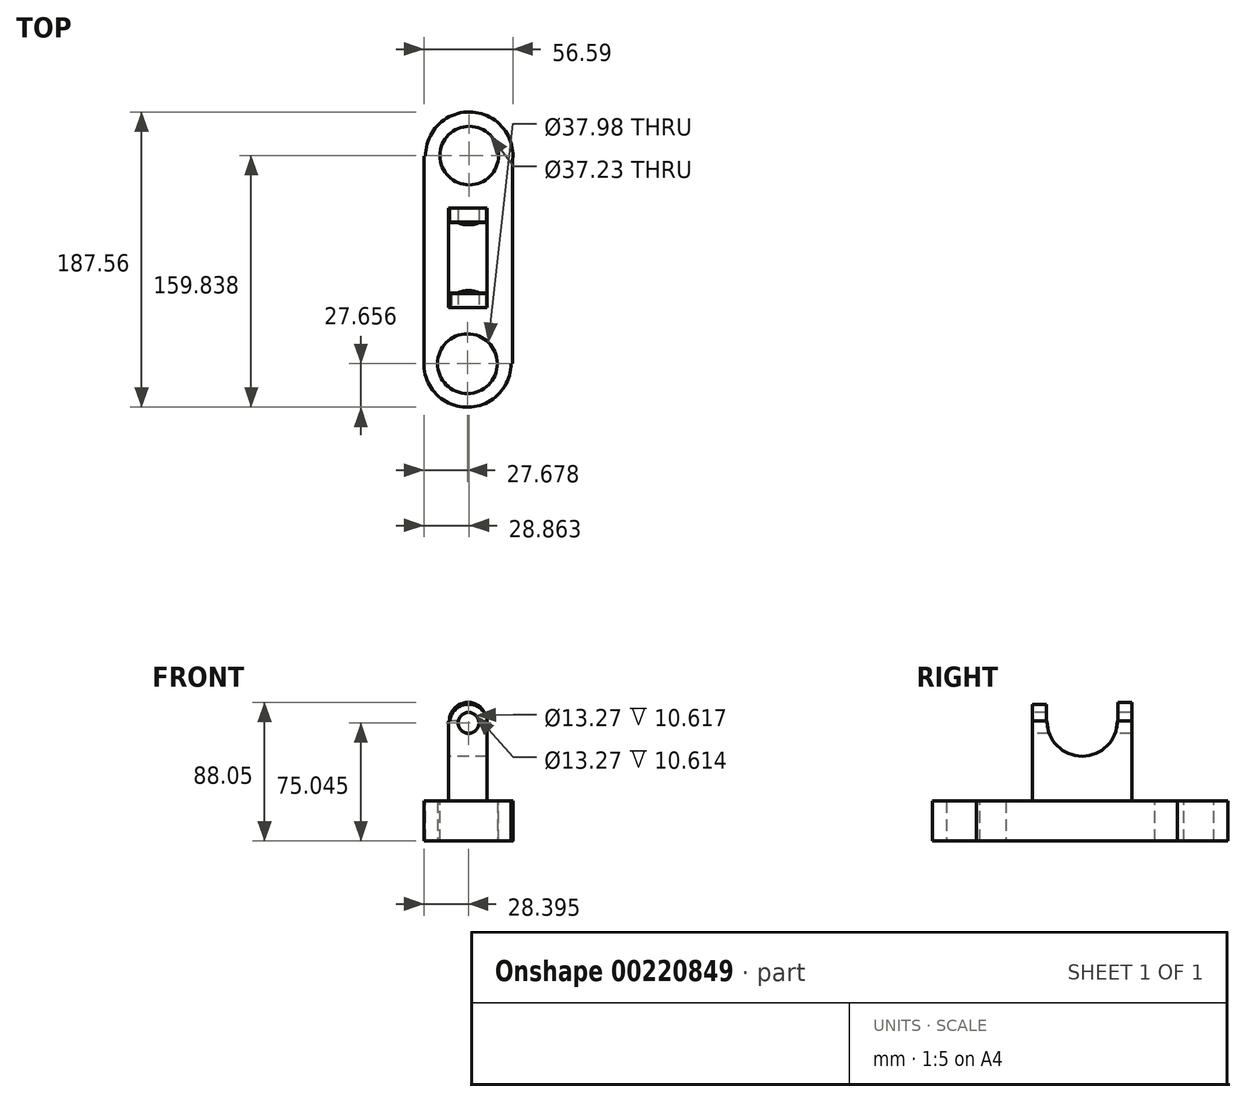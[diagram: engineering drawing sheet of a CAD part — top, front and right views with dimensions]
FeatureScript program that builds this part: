
annotation { "Feature Type Name" : "Feature", "Feature Type Description" : "" }
export const myFeature = defineFeature(function(context is Context, id is Id, definition is map)
    precondition{}
    {
        {
            var Q0;
            Q0=qCreatedBy(makeId("Top.planeOp"),FACE);
            var sketch = newSketch(context, id + "F0", { "sketchPlane" : qUnion([Q0])});
            skLineSegment(sketch, "E0.bottom", {"start": v(-15.7, 58.3) * mm, "end": v(40.4, 58.3) * mm});
            skLineSegment(sketch, "E0.top", {"start": v(-15.7, -73.54) * mm, "end": v(40.4, -73.54) * mm});
            skLineSegment(sketch, "E0.left", {"start": v(-15.7, 58.3) * mm, "end": v(-15.7, -73.54) * mm});
            skLineSegment(sketch, "E0.right", {"start": v(40.4, 58.3) * mm, "end": v(40.4, -73.54) * mm});
            skSolve(sketch);
        }
        {
            var Q0;
            Q0 = qSketchRegion(id + "F0", true);
            extrude(context, id + "F1", {"entities" : qUnion([Q0]), "depth" : 25.4 * mm});
        }
        {
            var Q0;
            Q0=makeQuery(id+"F1.opExtrude","CAP_FACE",FACE,{"disambiguationData":[OSD([sQuery(id+"F0.wireOp",EDGE,"E0.bottom"),sQuery(id+"F0.wireOp",EDGE,"E0.top"),sQuery(id+"F0.wireOp",EDGE,"E0.left"),sQuery(id+"F0.wireOp",EDGE,"E0.right")])],"isStart":false});
            var sketch = newSketch(context, id + "F2", { "sketchPlane" : qUnion([Q0])});
            skSolve(sketch);
        }
        {
            var Q0;
            Q0=makeQuery(id+"F2.imprint","IMPRINT",FACE,{"disambiguationData":[TD([[makeQuery(id+"F2.imprint","IMPRINT",EDGE,{"derivedFrom":makeQuery(id+"F1.opExtrude","CAP_EDGE",EDGE,{"disambiguationData":[OSD([sQuery(id+"F0.wireOp",EDGE,"E0.bottom")])],"isStart":false})}),-1.0]])]});
            var sketch = newSketch(context, id + "F3", { "sketchPlane" : qUnion([Q0])});
            skCircle(sketch, "E1", {"center": v(11.78, 40.06) * mm, "radius": 8.7 * mm});
            skSolve(sketch);
        }
        {
            var Q0;
            Q0 = qSketchRegion(id + "F3", true);
            extrude(context, id + "F4", {"entities" : qUnion([Q0]), "operationType" : NewBodyOperationType.REMOVE, "oppositeDirection" : true, "depth" : 25.4 * mm});
        }
        {
            var Q0;
            Q0=makeQuery(id+"F2.imprint","IMPRINT",FACE,{"disambiguationData":[TD([[makeQuery(id+"F2.imprint","IMPRINT",EDGE,{"derivedFrom":makeQuery(id+"F1.opExtrude","CAP_EDGE",EDGE,{"disambiguationData":[OSD([sQuery(id+"F0.wireOp",EDGE,"E0.bottom")])],"isStart":false})}),-1.0]])]});
            var sketch = newSketch(context, id + "F5", { "sketchPlane" : qUnion([Q0])});
            skCircle(sketch, "E2", {"center": v(11.31, -57.84) * mm, "radius": 8.85 * mm});
            skSolve(sketch);
        }
        {
            var Q0;
            Q0 = qSketchRegion(id + "F5", true);
            extrude(context, id + "F6", {"entities" : qUnion([Q0]), "operationType" : NewBodyOperationType.REMOVE, "oppositeDirection" : true, "depth" : 25.4 * mm});
        }
        {
            var Q0;
            Q0=makeQuery(id+"F2.imprint","IMPRINT",FACE,{"disambiguationData":[TD([[makeQuery(id+"F2.imprint","IMPRINT",EDGE,{"derivedFrom":makeQuery(id+"F1.opExtrude","CAP_EDGE",EDGE,{"disambiguationData":[OSD([sQuery(id+"F0.wireOp",EDGE,"E0.bottom")])],"isStart":false})}),-1.0]])]});
            var sketch = newSketch(context, id + "F7", { "sketchPlane" : qUnion([Q0])});
            skLineSegment(sketch, "E3.bottom", {"start": v(0, 25.28) * mm, "end": v(24.48, 25.28) * mm});
            skLineSegment(sketch, "E3.top", {"start": v(0, -37.75) * mm, "end": v(24.48, -37.75) * mm});
            skLineSegment(sketch, "E3.left", {"start": v(0, 25.28) * mm, "end": v(0, -37.75) * mm});
            skLineSegment(sketch, "E3.right", {"start": v(24.48, 25.28) * mm, "end": v(24.48, -37.75) * mm});
            skSolve(sketch);
        }
        {
            var Q0;
            Q0 = qSketchRegion(id + "F7", true);
            extrude(context, id + "F8", {"entities" : qUnion([Q0]), "operationType" : NewBodyOperationType.ADD, "depth" : 50.8 * mm});
        }
        {
            var Q0;
            Q0=makeQuery(id+"F8.opExtrude","SWEPT_FACE",FACE,{"disambiguationData":[OSD([sQuery(id+"F7.wireOp",EDGE,"E3.left")])]});
            var sketch = newSketch(context, id + "F9", { "sketchPlane" : qUnion([Q0])});
            skCircle(sketch, "E4", {"center": v(6.23, 76.2) * mm, "radius": 22.3 * mm});
            skSolve(sketch);
        }
        {
            var Q0;
            Q0 = qSketchRegion(id + "F9", true);
            extrude(context, id + "F10", {"entities" : qUnion([Q0]), "operationType" : NewBodyOperationType.ADD, "depth" : 76.2 * mm});
        }
        {
            var Q0;
            Q0=makeQuery(id+"F10.opExtrude","CAP_FACE",FACE,{"disambiguationData":[OSD([sQuery(id+"F9.wireOp",EDGE,"E4")])],"isStart":false});
            extrude(context, id + "F11", {"entities" : qUnion([Q0]), "operationType" : NewBodyOperationType.REMOVE, "oppositeDirection" : true, "depth" : 127 * mm});
        }
        {
            var Q0;
            Q0=makeQuery(id+"F8.opExtrude","SWEPT_FACE",FACE,{"disambiguationData":[OSD([sQuery(id+"F7.wireOp",EDGE,"E3.top")])]});
            var sketch = newSketch(context, id + "F12", { "sketchPlane" : qUnion([Q0])});
            skCircle(sketch, "E5", {"center": v(12.58, 75.05) * mm, "radius": 10.75 * mm});
            skCircle(sketch, "E6", {"center": v(12.58, 75.05) * mm, "radius": 11.86 * mm});
            skSolve(sketch);
        }
        {
            var Q0;
            Q0 = qSketchRegion(id + "F12", true);
            extrude(context, id + "F13", {"entities" : qUnion([Q0]), "operationType" : NewBodyOperationType.ADD, "oppositeDirection" : true, "depth" : 8.9 * mm});
        }
        {
            var Q0;
            Q0=makeQuery(id+"F13.boolean.opBoolean","MERGE",FACE,{"derivedFrom":[makeQuery(id+"F8.opExtrude","SWEPT_FACE",FACE,{"disambiguationData":[OSD([sQuery(id+"F7.wireOp",EDGE,"E3.top")])]}),makeQuery(id+"F13.opExtrude","CAP_FACE",FACE,{"disambiguationData":[OSD([sQuery(id+"F12.wireOp",EDGE,"E5"),sQuery(id+"F12.wireOp",EDGE,"E6")])],"isStart":true})]});
            var sketch = newSketch(context, id + "F14", { "sketchPlane" : qUnion([Q0])});
            skCircle(sketch, "E7", {"center": v(12.58, 76.2) * mm, "radius": 10.67 * mm});
            skSolve(sketch);
        }
        {
            var Q0;
            Q0 = qSketchRegion(id + "F14", true);
            extrude(context, id + "F15", {"entities" : qUnion([Q0]), "operationType" : NewBodyOperationType.ADD, "oppositeDirection" : true, "depth" : 8.9 * mm});
        }
        {
            var Q0;
            Q0=makeQuery(id+"F8.opExtrude","SWEPT_FACE",FACE,{"disambiguationData":[OSD([sQuery(id+"F7.wireOp",EDGE,"E3.bottom")])]});
            var sketch = newSketch(context, id + "F16", { "sketchPlane" : qUnion([Q0])});
            skCircle(sketch, "E8", {"center": v(-12.24, 76.2) * mm, "radius": 11.85 * mm});
            skSolve(sketch);
        }
        {
            var Q0;
            Q0 = qSketchRegion(id + "F16", true);
            extrude(context, id + "F17", {"entities" : qUnion([Q0]), "operationType" : NewBodyOperationType.ADD, "oppositeDirection" : true, "depth" : 8.9 * mm});
        }
        {
            var Q0;
            Q0=makeQuery(id+"F15.boolean.opBoolean","MERGE",FACE,{"derivedFrom":[makeQuery(id+"F13.boolean.opBoolean","MERGE",FACE,{"derivedFrom":[makeQuery(id+"F8.opExtrude","SWEPT_FACE",FACE,{"disambiguationData":[OSD([sQuery(id+"F7.wireOp",EDGE,"E3.top")])]}),makeQuery(id+"F13.opExtrude","CAP_FACE",FACE,{"disambiguationData":[OSD([sQuery(id+"F12.wireOp",EDGE,"E5"),sQuery(id+"F12.wireOp",EDGE,"E6")])],"isStart":true})]}),makeQuery(id+"F15.opExtrude","CAP_FACE",FACE,{"disambiguationData":[OSD([sQuery(id+"F14.wireOp",EDGE,"E7")])],"isStart":true})]});
            var sketch = newSketch(context, id + "F18", { "sketchPlane" : qUnion([Q0])});
            skCircle(sketch, "E9", {"center": v(12.58, 76.2) * mm, "radius": 5.51 * mm});
            skSolve(sketch);
        }
        {
            var Q0;
            Q0 = qSketchRegion(id + "F18", true);
            extrude(context, id + "F19", {"entities" : qUnion([Q0]), "operationType" : NewBodyOperationType.REMOVE, "depth" : 304.8 * mm});
        }
        {
            var Q0;
            Q0=makeQuery(id+"F15.boolean.opBoolean","MERGE",FACE,{"derivedFrom":[makeQuery(id+"F13.boolean.opBoolean","MERGE",FACE,{"derivedFrom":[makeQuery(id+"F8.opExtrude","SWEPT_FACE",FACE,{"disambiguationData":[OSD([sQuery(id+"F7.wireOp",EDGE,"E3.top")])]}),makeQuery(id+"F13.opExtrude","CAP_FACE",FACE,{"disambiguationData":[OSD([sQuery(id+"F12.wireOp",EDGE,"E5"),sQuery(id+"F12.wireOp",EDGE,"E6")])],"isStart":true})]}),makeQuery(id+"F15.opExtrude","CAP_FACE",FACE,{"disambiguationData":[OSD([sQuery(id+"F14.wireOp",EDGE,"E7")])],"isStart":true})]});
            var sketch = newSketch(context, id + "F20", { "sketchPlane" : qUnion([Q0])});
            skCircle(sketch, "E10", {"center": v(12.58, 75.05) * mm, "radius": 6.63 * mm});
            skSolve(sketch);
        }
        {
            var Q0;
            Q0 = qSketchRegion(id + "F20", true);
            extrude(context, id + "F21", {"entities" : qUnion([Q0]), "operationType" : NewBodyOperationType.REMOVE, "oppositeDirection" : true, "depth" : 304.8 * mm});
        }
        {
            var Q0;
            Q0=makeQuery(id+"F2.imprint","IMPRINT",FACE,{"disambiguationData":[TD([[makeQuery(id+"F2.imprint","IMPRINT",EDGE,{"derivedFrom":makeQuery(id+"F1.opExtrude","CAP_EDGE",EDGE,{"disambiguationData":[OSD([sQuery(id+"F0.wireOp",EDGE,"E0.bottom")])],"isStart":false})}),-1.0]])]});
            var sketch = newSketch(context, id + "F22", { "sketchPlane" : qUnion([Q0])});
            skCircle(sketch, "E11", {"center": v(12, -73.78) * mm, "radius": 27.02 * mm});
            skSolve(sketch);
        }
        {
            var Q0;
            Q0=sQuery(id+"F22.wireOp",EDGE,"E11");
            extrude(context, id + "F23", {"bodyType" : ToolBodyType.SURFACE, "surfaceEntities" : qUnion([Q0]), "oppositeDirection" : true, "depth" : 25.4 * mm});
        }
        {
            var Q0;
            Q0=makeQuery(id+"F2.imprint","IMPRINT",FACE,{"disambiguationData":[TD([[makeQuery(id+"F2.imprint","IMPRINT",EDGE,{"derivedFrom":makeQuery(id+"F1.opExtrude","CAP_EDGE",EDGE,{"disambiguationData":[OSD([sQuery(id+"F0.wireOp",EDGE,"E0.bottom")])],"isStart":false})}),-1.0]])]});
            var sketch = newSketch(context, id + "F24", { "sketchPlane" : qUnion([Q0])});
            skCircle(sketch, "E12", {"center": v(11.87, -73.52) * mm, "radius": 18.97 * mm});
            skCircle(sketch, "E13", {"center": v(11.87, -73.52) * mm, "radius": 27.68 * mm});
            skSolve(sketch);
        }
        {
            var Q0;
            Q0 = qSketchRegion(id + "F24", true);
            extrude(context, id + "F25", {"entities" : qUnion([Q0]), "operationType" : NewBodyOperationType.ADD, "oppositeDirection" : true, "depth" : 25.4 * mm});
        }
        {
            var Q0;
            Q0=makeQuery(id+"F2.imprint","IMPRINT",FACE,{"disambiguationData":[TD([[makeQuery(id+"F2.imprint","IMPRINT",EDGE,{"derivedFrom":makeQuery(id+"F1.opExtrude","CAP_EDGE",EDGE,{"disambiguationData":[OSD([sQuery(id+"F0.wireOp",EDGE,"E0.bottom")])],"isStart":false})}),-1.0]])]});
            var sketch = newSketch(context, id + "F26", { "sketchPlane" : qUnion([Q0])});
            skLineSegment(sketch, "E14.bottom", {"start": v(12.84, -71.37) * mm, "end": v(0, -71.37) * mm});
            skLineSegment(sketch, "E14.top", {"start": v(12.84, -47.36) * mm, "end": v(0, -47.36) * mm});
            skLineSegment(sketch, "E14.left", {"start": v(12.84, -71.37) * mm, "end": v(12.84, -47.36) * mm});
            skLineSegment(sketch, "E14.right", {"start": v(0, -71.37) * mm, "end": v(0, -47.36) * mm});
            skLineSegment(sketch, "E15.bottom", {"start": v(12.84, -47.36) * mm, "end": v(20.45, -47.36) * mm});
            skLineSegment(sketch, "E15.top", {"start": v(12.84, -47.36) * mm, "end": v(20.45, -47.36) * mm});
            skLineSegment(sketch, "E15.left", {"start": v(12.84, -47.36) * mm, "end": v(12.84, -47.36) * mm});
            skLineSegment(sketch, "E15.right", {"start": v(20.45, -47.36) * mm, "end": v(20.45, -47.36) * mm});
            skLineSegment(sketch, "E16.top", {"start": v(12.84, -71.6) * mm, "end": v(20.45, -71.6) * mm});
            skLineSegment(sketch, "E16.left", {"start": v(12.84, -47.36) * mm, "end": v(12.84, -71.6) * mm});
            skLineSegment(sketch, "E16.right", {"start": v(20.45, -47.36) * mm, "end": v(20.45, -71.6) * mm});
            skSolve(sketch);
        }
        {
            var Q0;
            Q0 = qSketchRegion(id + "F26", true);
            extrude(context, id + "F27", {"entities" : qUnion([Q0]), "operationType" : NewBodyOperationType.ADD, "oppositeDirection" : true, "depth" : 25.4 * mm});
        }
        {
            var Q0;
            Q0=makeQuery(id+"F27.boolean.opBoolean","MERGE",FACE,{"derivedFrom":[makeQuery(id+"F25.boolean.opBoolean","MERGE",FACE,{"derivedFrom":[makeQuery(id+"F1.opExtrude","CAP_FACE",FACE,{"disambiguationData":[OSD([sQuery(id+"F0.wireOp",EDGE,"E0.bottom"),sQuery(id+"F0.wireOp",EDGE,"E0.top"),sQuery(id+"F0.wireOp",EDGE,"E0.left"),sQuery(id+"F0.wireOp",EDGE,"E0.right")])],"isStart":true}),makeQuery(id+"F25.opExtrude","CAP_FACE",FACE,{"disambiguationData":[OSD([sQuery(id+"F24.wireOp",EDGE,"E12"),sQuery(id+"F24.wireOp",EDGE,"E13")])],"isStart":false})]}),makeQuery(id+"F27.opExtrude","CAP_FACE",FACE,{"disambiguationData":[OSD([sQuery(id+"F26.wireOp",EDGE,"E14.bottom"),sQuery(id+"F26.wireOp",EDGE,"E14.top"),sQuery(id+"F26.wireOp",EDGE,"E14.right"),sQuery(id+"F26.wireOp",EDGE,"E15.bottom"),sQuery(id+"F26.wireOp",EDGE,"E16.top"),sQuery(id+"F26.wireOp",EDGE,"E16.left"),sQuery(id+"F26.wireOp",EDGE,"E16.right")])],"isStart":false})]});
            var sketch = newSketch(context, id + "F28", { "sketchPlane" : qUnion([Q0])});
            skCircle(sketch, "E17", {"center": v(11.87, 73.54) * mm, "radius": 18.99 * mm});
            skSolve(sketch);
        }
        {
            var Q0;
            Q0 = qSketchRegion(id + "F28", true);
            extrude(context, id + "F29", {"entities" : qUnion([Q0]), "operationType" : NewBodyOperationType.REMOVE, "oppositeDirection" : true, "depth" : 25.4 * mm});
        }
        {
            var Q0;
            Q0=makeQuery(id+"F2.imprint","IMPRINT",FACE,{"disambiguationData":[TD([[makeQuery(id+"F2.imprint","IMPRINT",EDGE,{"derivedFrom":makeQuery(id+"F1.opExtrude","CAP_EDGE",EDGE,{"disambiguationData":[OSD([sQuery(id+"F0.wireOp",EDGE,"E0.bottom")])],"isStart":false})}),-1.0]])]});
            var sketch = newSketch(context, id + "F30", { "sketchPlane" : qUnion([Q0])});
            skCircle(sketch, "E18", {"center": v(13.05, 58.64) * mm, "radius": 27.73 * mm});
            skSolve(sketch);
        }
        {
            var Q0;
            Q0 = qSketchRegion(id + "F30", true);
            extrude(context, id + "F31", {"entities" : qUnion([Q0]), "operationType" : NewBodyOperationType.ADD, "oppositeDirection" : true, "depth" : 25.4 * mm});
        }
        {
            var Q0;
            Q0=makeQuery(id+"F31.boolean.opBoolean","MERGE",FACE,{"derivedFrom":[makeQuery(id+"F27.boolean.opBoolean","MERGE",FACE,{"derivedFrom":[makeQuery(id+"F25.boolean.opBoolean","MERGE",FACE,{"derivedFrom":[makeQuery(id+"F1.opExtrude","CAP_FACE",FACE,{"disambiguationData":[OSD([sQuery(id+"F0.wireOp",EDGE,"E0.bottom"),sQuery(id+"F0.wireOp",EDGE,"E0.top"),sQuery(id+"F0.wireOp",EDGE,"E0.left"),sQuery(id+"F0.wireOp",EDGE,"E0.right")])],"isStart":true}),makeQuery(id+"F25.opExtrude","CAP_FACE",FACE,{"disambiguationData":[OSD([sQuery(id+"F24.wireOp",EDGE,"E12"),sQuery(id+"F24.wireOp",EDGE,"E13")])],"isStart":false})]}),makeQuery(id+"F27.opExtrude","CAP_FACE",FACE,{"disambiguationData":[OSD([sQuery(id+"F26.wireOp",EDGE,"E14.bottom"),sQuery(id+"F26.wireOp",EDGE,"E14.top"),sQuery(id+"F26.wireOp",EDGE,"E14.right"),sQuery(id+"F26.wireOp",EDGE,"E15.bottom"),sQuery(id+"F26.wireOp",EDGE,"E16.top"),sQuery(id+"F26.wireOp",EDGE,"E16.left"),sQuery(id+"F26.wireOp",EDGE,"E16.right")])],"isStart":false})]}),makeQuery(id+"F31.opExtrude","CAP_FACE",FACE,{"disambiguationData":[OSD([sQuery(id+"F30.wireOp",EDGE,"E18")])],"isStart":false})]});
            var sketch = newSketch(context, id + "F32", { "sketchPlane" : qUnion([Q0])});
            skCircle(sketch, "E19", {"center": v(13.05, -58.64) * mm, "radius": 19.33 * mm});
            skSolve(sketch);
        }
        {
            var Q0;
            Q0 = qSketchRegion(id + "F32", true);
            extrude(context, id + "F33", {"entities" : qUnion([Q0]), "operationType" : NewBodyOperationType.ADD, "oppositeDirection" : true, "depth" : 25.4 * mm});
        }
        {
            var Q0;
            Q0=makeQuery(id+"F31.boolean.opBoolean","MERGE",FACE,{"derivedFrom":[makeQuery(id+"F27.boolean.opBoolean","MERGE",FACE,{"derivedFrom":[makeQuery(id+"F25.boolean.opBoolean","MERGE",FACE,{"derivedFrom":[makeQuery(id+"F1.opExtrude","CAP_FACE",FACE,{"disambiguationData":[OSD([sQuery(id+"F0.wireOp",EDGE,"E0.bottom"),sQuery(id+"F0.wireOp",EDGE,"E0.top"),sQuery(id+"F0.wireOp",EDGE,"E0.left"),sQuery(id+"F0.wireOp",EDGE,"E0.right")])],"isStart":false}),makeQuery(id+"F25.opExtrude","CAP_FACE",FACE,{"disambiguationData":[OSD([sQuery(id+"F24.wireOp",EDGE,"E12"),sQuery(id+"F24.wireOp",EDGE,"E13")])],"isStart":true})]}),makeQuery(id+"F27.opExtrude","CAP_FACE",FACE,{"disambiguationData":[OSD([sQuery(id+"F26.wireOp",EDGE,"E14.bottom"),sQuery(id+"F26.wireOp",EDGE,"E14.top"),sQuery(id+"F26.wireOp",EDGE,"E14.right"),sQuery(id+"F26.wireOp",EDGE,"E15.bottom"),sQuery(id+"F26.wireOp",EDGE,"E16.top"),sQuery(id+"F26.wireOp",EDGE,"E16.left"),sQuery(id+"F26.wireOp",EDGE,"E16.right")])],"isStart":true})]}),makeQuery(id+"F31.opExtrude","CAP_FACE",FACE,{"disambiguationData":[OSD([sQuery(id+"F30.wireOp",EDGE,"E18")])],"isStart":true})]});
            var sketch = newSketch(context, id + "F34", { "sketchPlane" : qUnion([Q0])});
            skCircle(sketch, "E20", {"center": v(13.05, 58.64) * mm, "radius": 18.62 * mm});
            skSolve(sketch);
        }
        {
            var Q0;
            Q0 = qSketchRegion(id + "F34", true);
            extrude(context, id + "F35", {"entities" : qUnion([Q0]), "operationType" : NewBodyOperationType.REMOVE, "oppositeDirection" : true, "depth" : 25.4 * mm});
        }
    });
